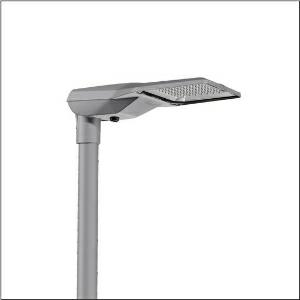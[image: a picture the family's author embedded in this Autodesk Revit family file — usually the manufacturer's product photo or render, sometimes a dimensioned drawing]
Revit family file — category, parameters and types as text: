
# Revit family: streetlight_sl_21_midi___p0_5a_5xe3v33r08mb_b2b8
name_source: partatom
category: Lighting Fixtures
units: mm (PartAtom-declared; Revit-internal decimal feet)

## family parameters
Cut with Voids When Loaded = No
Host = Face
Light Source = No
Part Type = Normal
Room Calculation Point = No
Round Connector Dimension = Use Diameter
Shared = No

## types (1)
- --- (1 x LED, 17960 lm, 136 W, 3000K)
    Apparent Load = 136 VA
    CIE Flux Codes = 37 73 96 100 100
    Color Rendering = 70
    Color Temperature = 3000K
    Default Elevation = 1800 mm
    Description = Streetlight SL 21 midi, mast luminaire, primary light control with lens, of PMMA, primary optical cover: cover, of toughened safety glass, transparent, light distribution: P0.5a, light emission: direct distribution, primary light characteristic: asymmetric, installation type: post-top, side-entry, LED, High Power LED, rated luminous flux: 17.960lm, luminous efficacy: 132lm/W, light colour: 730, colour temperature: 3000K, control gear: D4i, control: pre-setting: logarithmic dimming characteristic, flexible luminous flux parameterisation, time-dependent luminous flux control, constant luminous flux control, overheat protection, mains connection: 230..240V, AC, 50/60Hz, start of lifetime: 136W, end of service life: 142W, reduction: 61W, luminaire housing, of diecast aluminium, powder-coated, Siteco® metallic grey (DB 702S), corrosivity category C5 mid according to DIN EN ISO 12944, multi-level sealing system, sealing non-destructively replaceable, inclination adjustable: 0°, 5°, 10°, 15°, please order mast flange separately, length: 644mm, width: 335mm, height: 110mm, mast flange for spigot size: 42mm (side-entry): 5XC10008XM4, 60/48mm (side-entry/post-top): 5XC10108XM2, 76/60mm (side-entry/post-top): 5XC10108XM1, mounting height: 4..8m, Smart Interface below, protection rating (complete): IP66, insulation class (complete): insulation class II (safety insulation), certification: CE, ENEC, ENEC+, VDE, impact resistance: IK10, permissible operating ambient temperature for outdoor applications: -40..+50°C, standard-compliant lighting for roads and squares, packaging unit: 1 piece

Light Distribution: P0.5a
    Height = 111 mm
    Lamp = 1 x LED
    Lamp Light Flux = 17960 lm
    Lamp Power = 136 W
    Lamp count = 1
    Length = 644 mm
    Luminous efficacy = 132 lm/W
    Manufacturer = Siteco
    ModVariant = No
    Model = 5XE3V33R08MB
    Number of Poles = 1
    OnlyDefault = Yes
    Power Factor = 1
    Product Name = Streetlight SL 21 midi | P0.5a
    Product group = mast luminaire | pylon top
    ProductGroupID = 6100
    Protection Class = Protection class II
    Protection Degree = IP 66
    RLX_Detail_Level = 1
    RLX_Emergency_Light_Flux = 0 lm
    RLX_Emergency_Type = 0
    RLX_Emergency_Type_DB = No
    RlxData = <blob elided: 26517 chars, md5=a9d04684>
    Socket = socket
    Standby Power = 0 W
    System Light Flux = 17960 lm
    System Power = 136 W
    Type Comments = factory setting: luminous flux: 100 % | dim-lin: 254 | 695 mA
    Type Image = l_1004300.jpg
    URL = http://relux.com
    VarID = @adj_069952
    Voltage = 0 V
    Weight = 0.00 kg
    Width = 336 mm

## geometry (parser evidence)
native form markers: Blend x4, Sweep x11
no freeform markers — native parametric forms only
